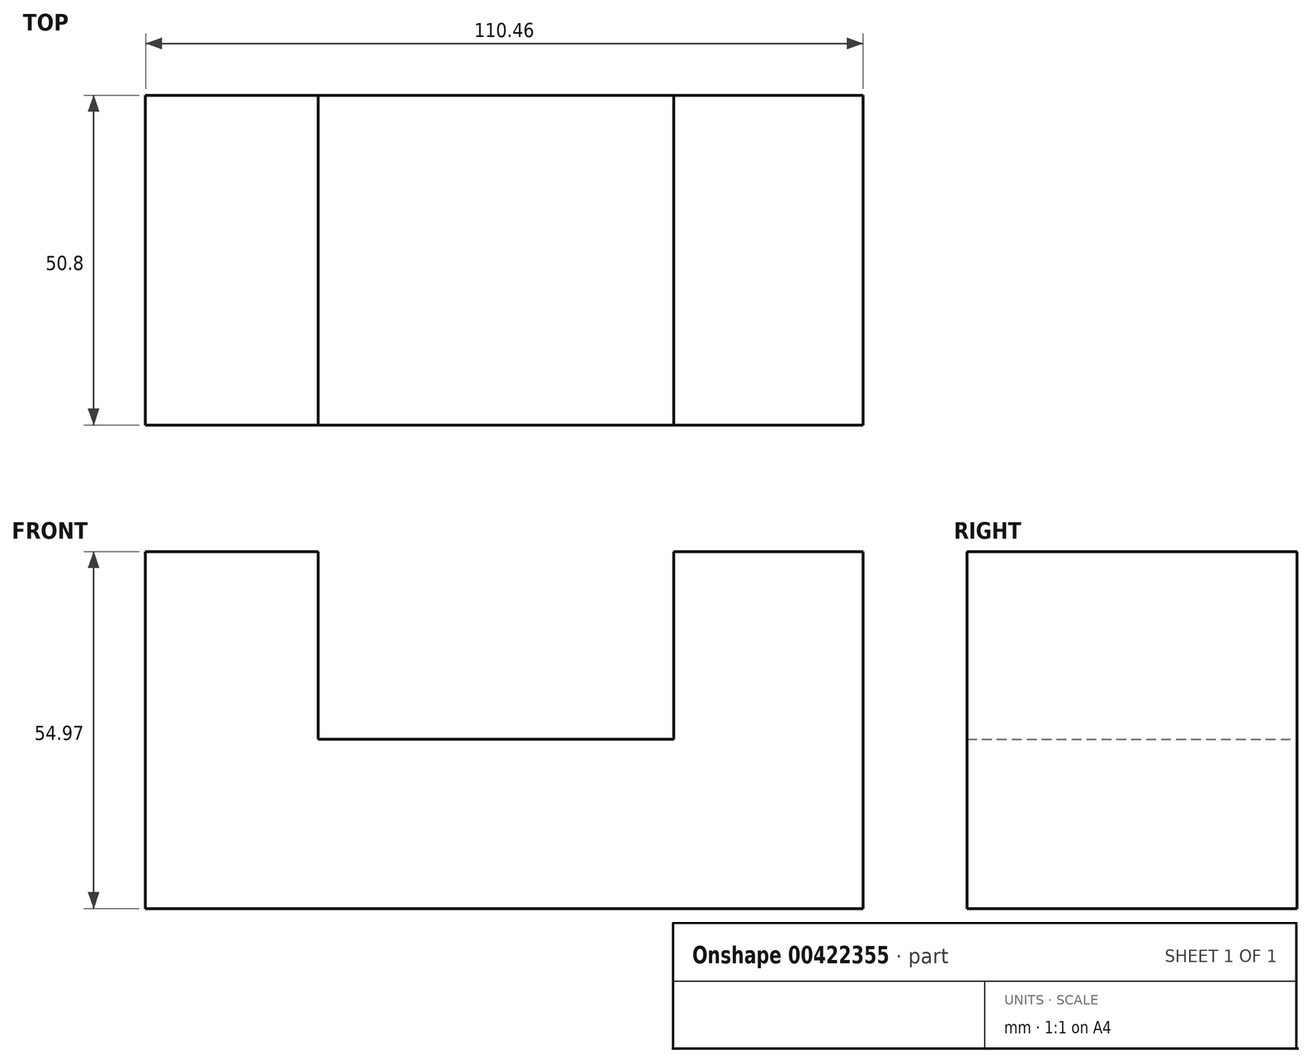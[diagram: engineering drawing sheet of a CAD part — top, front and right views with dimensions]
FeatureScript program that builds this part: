
annotation { "Feature Type Name" : "Feature", "Feature Type Description" : "" }
export const myFeature = defineFeature(function(context is Context, id is Id, definition is map)
    precondition{}
    {
        {
            var Q0;
            Q0=qCreatedBy(makeId("Front.planeOp"),FACE);
            var sketch = newSketch(context, id + "F0", { "sketchPlane" : qUnion([Q0])});
            skLineSegment(sketch, "E0", {"start": v(-55.5, 54.97) * mm, "end": v(-55.5, 0) * mm});
            skLineSegment(sketch, "E1", {"start": v(-55.5, 0) * mm, "end": v(0, 0) * mm});
            skLineSegment(sketch, "E2", {"start": v(0, 0) * mm, "end": v(0, 26.58) * mm});
            skLineSegment(sketch, "E3", {"start": v(-55.5, 54.97) * mm, "end": v(-28.9, 54.97) * mm});
            skLineSegment(sketch, "E4", {"start": v(-28.9, 54.97) * mm, "end": v(-28.9, 26.07) * mm});
            skLineSegment(sketch, "E5", {"start": v(-28.9, 26.07) * mm, "end": v(0, 26.07) * mm});
            skLineSegment(sketch, "E6", {"start": v(0, 26.07) * mm, "end": v(25.8, 26.07) * mm});
            skLineSegment(sketch, "E7", {"start": v(25.8, 26.07) * mm, "end": v(25.8, 54.97) * mm});
            skLineSegment(sketch, "E8", {"start": v(25.8, 54.97) * mm, "end": v(54.97, 54.97) * mm});
            skLineSegment(sketch, "E9", {"start": v(54.97, 54.97) * mm, "end": v(54.97, 0) * mm});
            skLineSegment(sketch, "E10", {"start": v(54.97, 0) * mm, "end": v(0, 0) * mm});
            skSolve(sketch);
        }
        {
            var Q0;
            Q0 = qSketchRegion(id + "F0", true);
            extrude(context, id + "F1", {"entities" : qUnion([Q0]), "depth" : 25.4 * mm});
        }
        {
            var Q0;
            Q0=makeQuery(id+"F1.opExtrude","CAP_FACE",FACE,{"disambiguationData":[OSD([sQuery(id+"F0.wireOp",EDGE,"E0"),sQuery(id+"F0.wireOp",EDGE,"E1"),sQuery(id+"F0.wireOp",EDGE,"E3"),sQuery(id+"F0.wireOp",EDGE,"E4"),sQuery(id+"F0.wireOp",EDGE,"E5"),sQuery(id+"F0.wireOp",EDGE,"E6"),sQuery(id+"F0.wireOp",EDGE,"E7"),sQuery(id+"F0.wireOp",EDGE,"E8"),sQuery(id+"F0.wireOp",EDGE,"E9"),sQuery(id+"F0.wireOp",EDGE,"E10")])],"isStart":false});
            extrude(context, id + "F2", {"entities" : qUnion([Q0]), "operationType" : NewBodyOperationType.ADD, "depth" : 25.4 * mm});
        }
    });
